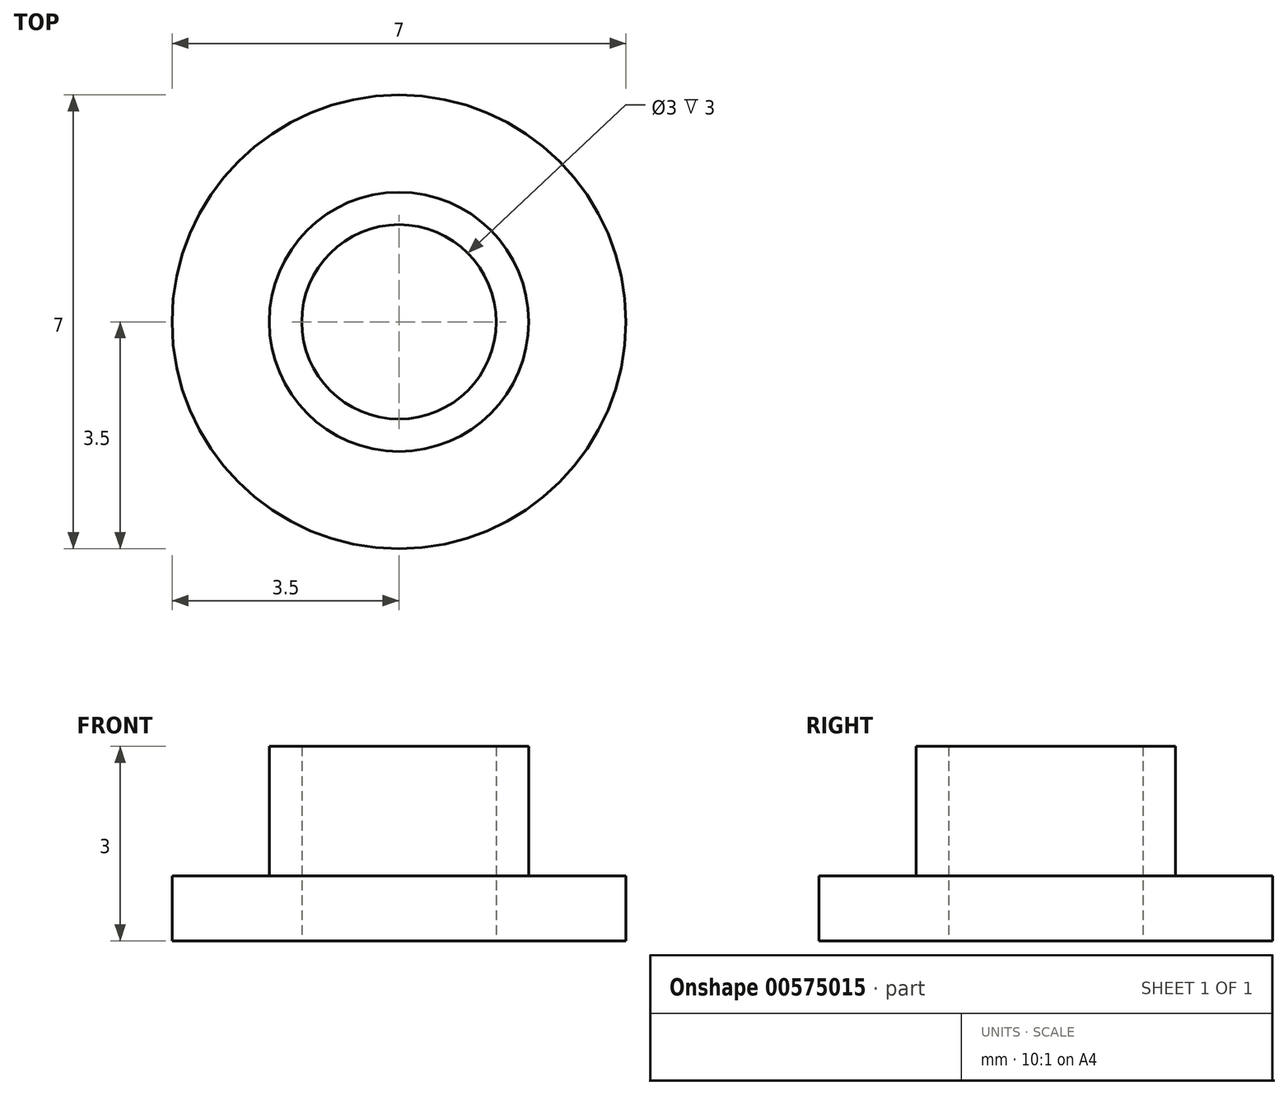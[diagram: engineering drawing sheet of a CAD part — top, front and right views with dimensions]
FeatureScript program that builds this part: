
annotation { "Feature Type Name" : "Feature", "Feature Type Description" : "" }
export const myFeature = defineFeature(function(context is Context, id is Id, definition is map)
    precondition{}
    {
        {
            var Q0;
            Q0=qCreatedBy(makeId("Top.planeOp"),FACE);
            var sketch = newSketch(context, id + "F0", { "sketchPlane" : qUnion([Q0])});
            skCircle(sketch, "E0", {"center": v(0, 0) * mm, "radius": 3.5 * mm});
            skCircle(sketch, "E1", {"center": v(0, 0) * mm, "radius": 2 * mm});
            skCircle(sketch, "E2", {"center": v(0, 0) * mm, "radius": 1.5 * mm});
            skSolve(sketch);
        }
        {
            var Q0;
            Q0 = qSketchRegion(id + "F0", true);
            extrude(context, id + "F1", {"entities" : qUnion([Q0]), "depth" : 1 * mm, "offsetDistance" : 25 * mm});
        }
        {
            var Q0;
            Q0=makeQuery(id+"F0.imprint","IMPRINT",FACE,{"disambiguationData":[TD([[makeQuery(id+"F0.imprint","IMPRINT",EDGE,{"derivedFrom":sQuery(id+"F0.wireOp",EDGE,"E1")}),1.0]])]});
            extrude(context, id + "F2", {"entities" : qUnion([Q0]), "operationType" : NewBodyOperationType.ADD, "depth" : 3 * mm, "offsetDistance" : 25 * mm});
        }
    });
